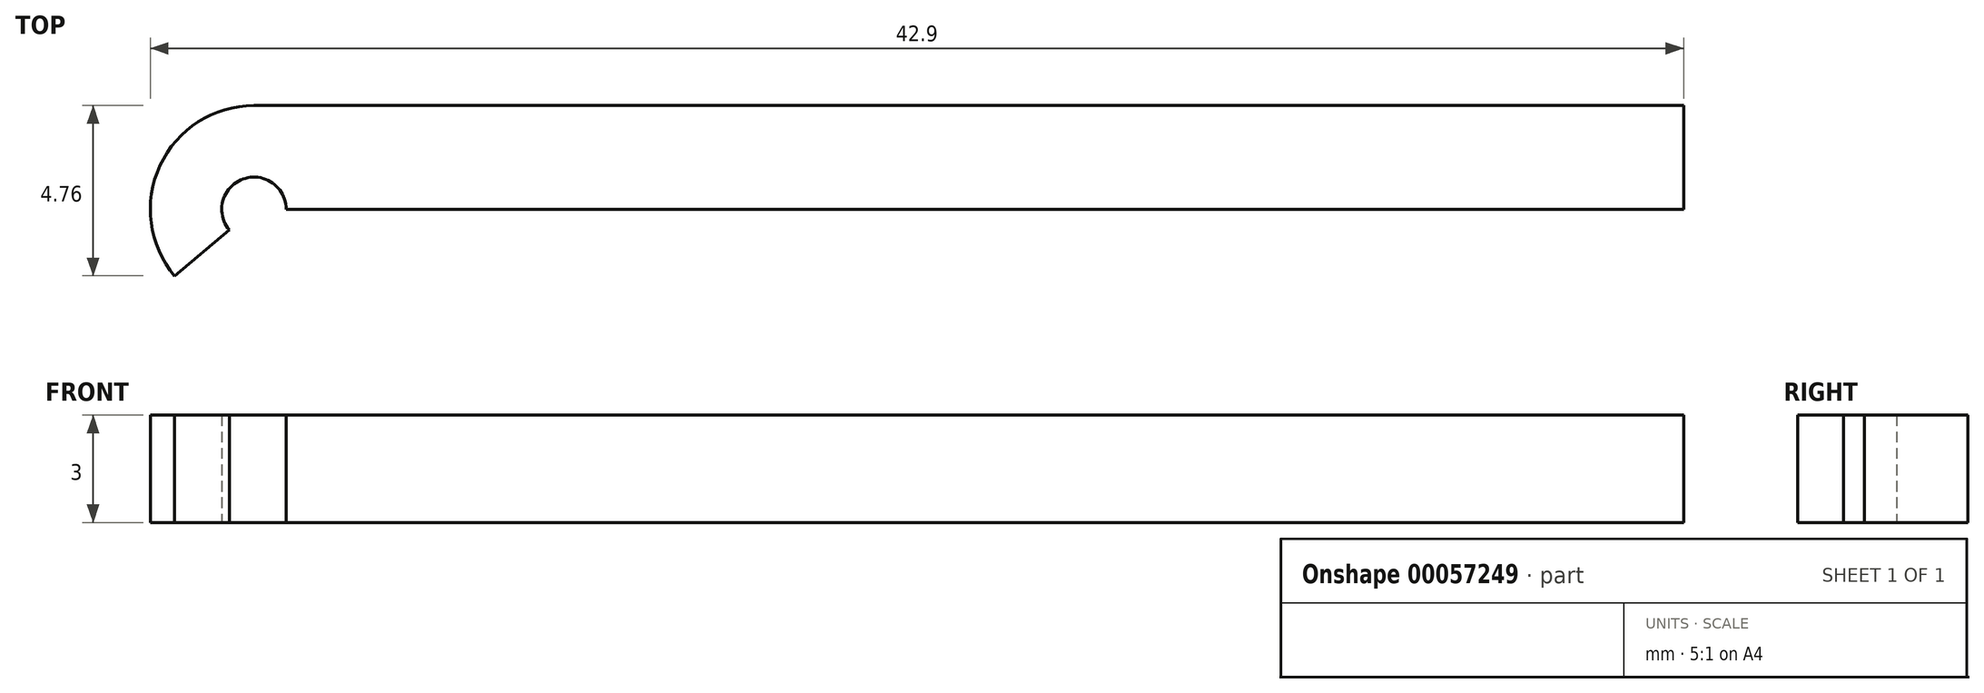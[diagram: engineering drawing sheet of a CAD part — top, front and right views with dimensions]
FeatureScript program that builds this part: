
annotation { "Feature Type Name" : "Feature", "Feature Type Description" : "" }
export const myFeature = defineFeature(function(context is Context, id is Id, definition is map)
    precondition{}
    {
        {
            var Q0;
            Q0=qCreatedBy(makeId("Top.planeOp"),FACE);
            var sketch = newSketch(context, id + "F0", { "sketchPlane" : qUnion([Q0])});
            skLineSegment(sketch, "E0", {"start": v(-40, 0) * mm, "end": v(40, 0) * mm, "construction": true});
            skCircle(sketch, "E1", {"center": v(-40, 0) * mm, "radius": 0.9 * mm});
            skArc(sketch, "E2.0", {"start": v(-40, 2.9) * mm, "mid": v(-42.05, -2.05) * mm, "end": v(-37.1, 0) * mm});
            skLineSegment(sketch, "E3", {"start": v(-40, 0) * mm, "end": v(-40.69, -0.58) * mm, "construction": true});
            skLineSegment(sketch, "E4", {"start": v(-40.69, -0.58) * mm, "end": v(-42.22, -1.86) * mm});
            skLineSegment(sketch, "E5", {"start": v(-40, 2.9) * mm, "end": v(0, 2.9) * mm});
            skLineSegment(sketch, "E6", {"start": v(-37.1, 0) * mm, "end": v(0, 0) * mm});
            skLineSegment(sketch, "E7", {"start": v(0, 0) * mm, "end": v(0, 2.9) * mm});
            skPoint(sketch, "E7.endSnap0", {"position": v(0, 0) * mm});
            skLineSegment(sketch, "E8", {"start": v(-37.1, 0) * mm, "end": v(-39.1, 0) * mm});
            skSolve(sketch);
        }
        {
            var Q0;
            {var subQ1=sQuery(id+"F0.wireOp",EDGE,"E4");Q0=makeQuery(id+"F0.imprint","IMPRINT",FACE,{"disambiguationData":[TD([[makeQuery(id+"F0.imprint","IMPRINT",EDGE,{"derivedFrom":subQ1}),-1.0]])]});}
            extrude(context, id + "F1", {"entities" : qUnion([Q0]), "depth" : 3 * mm});
        }
    });
